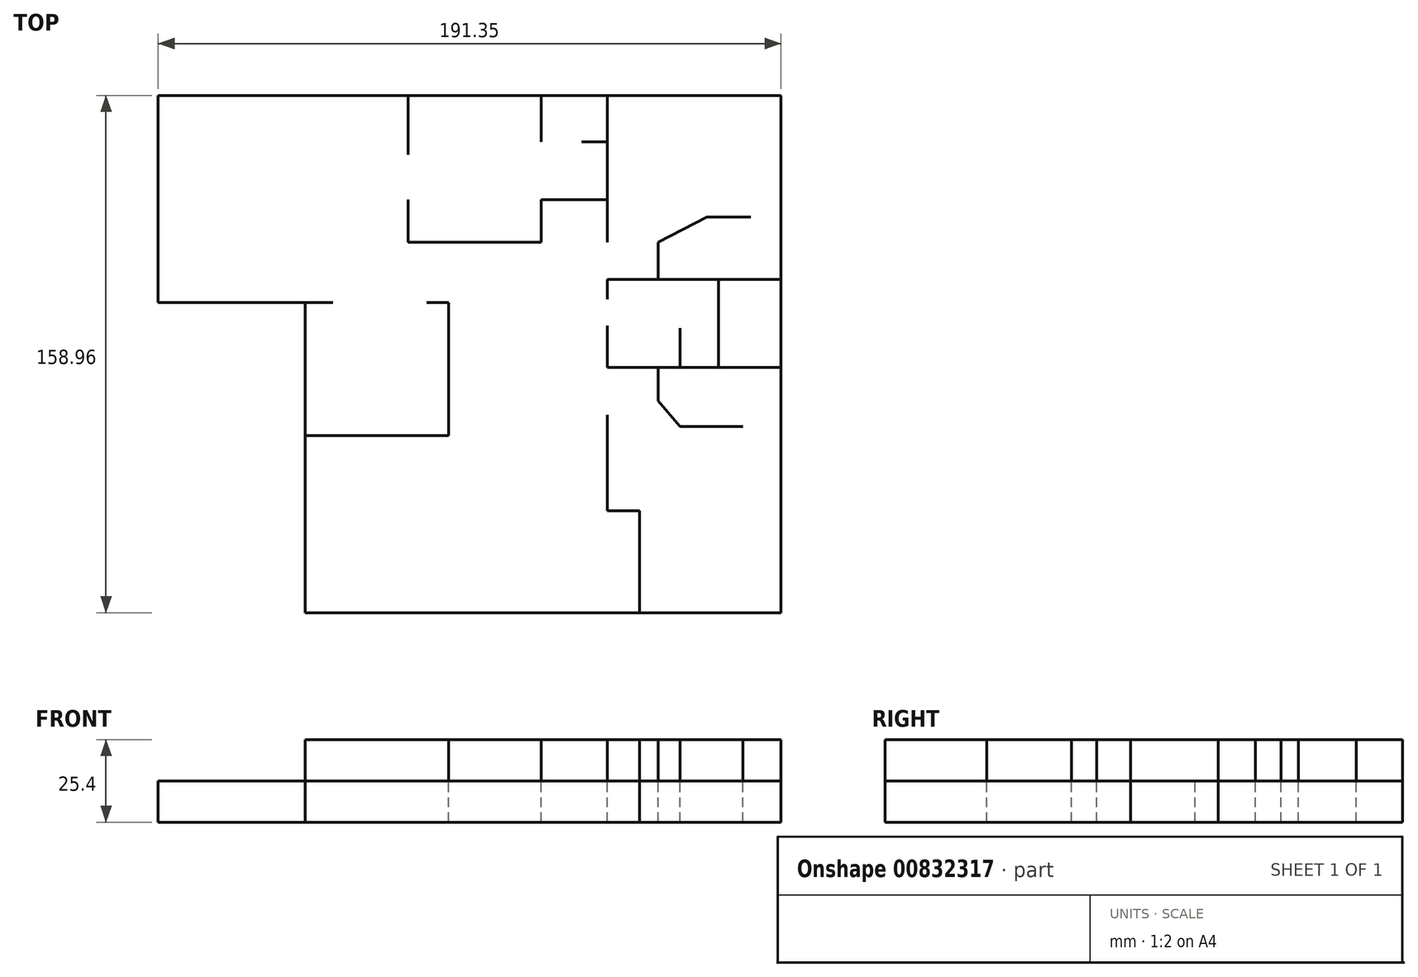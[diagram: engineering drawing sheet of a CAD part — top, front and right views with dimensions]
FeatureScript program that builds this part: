
annotation { "Feature Type Name" : "Feature", "Feature Type Description" : "" }
export const myFeature = defineFeature(function(context is Context, id is Id, definition is map)
    precondition{}
    {
        {
            var Q0;
            Q0=qCreatedBy(makeId("Top.planeOp"),FACE);
            var sketch = newSketch(context, id + "F0", { "sketchPlane" : qUnion([Q0])});
            skLineSegment(sketch, "E0", {"start": v(-96.38, 28.38) * mm, "end": v(94.97, 28.38) * mm});
            skLineSegment(sketch, "E1", {"start": v(94.97, 28.38) * mm, "end": v(94.97, -130.58) * mm});
            skLineSegment(sketch, "E2", {"start": v(94.97, -130.58) * mm, "end": v(-51.2, -130.58) * mm});
            skLineSegment(sketch, "E3", {"start": v(-51.2, -130.58) * mm, "end": v(-51.2, -35.27) * mm});
            skLineSegment(sketch, "E4", {"start": v(-51.2, -35.27) * mm, "end": v(-96.38, -35.27) * mm});
            skLineSegment(sketch, "E5", {"start": v(-96.38, -35.27) * mm, "end": v(-96.38, 28.38) * mm});
            skLineSegment(sketch, "E6", {"start": v(-51.2, -35.27) * mm, "end": v(-42.67, -35.27) * mm});
            skLineSegment(sketch, "E7", {"start": v(-51.2, -76.17) * mm, "end": v(-7.1, -76.17) * mm});
            skLineSegment(sketch, "E8", {"start": v(-7.1, -76.17) * mm, "end": v(-7.1, -35.27) * mm});
            skLineSegment(sketch, "E9", {"start": v(-7.1, -35.27) * mm, "end": v(-13.86, -35.27) * mm});
            skLineSegment(sketch, "E10", {"start": v(51.58, -99.29) * mm, "end": v(51.58, -130.58) * mm});
            skLineSegment(sketch, "E11", {"start": v(41.62, -99.29) * mm, "end": v(51.58, -99.29) * mm});
            skLineSegment(sketch, "E12", {"start": v(41.62, -69.77) * mm, "end": v(41.62, -99.29) * mm});
            skLineSegment(sketch, "E13", {"start": v(41.62, -99.29) * mm, "end": v(41.62, -69.77) * mm});
            skLineSegment(sketch, "E14", {"start": v(41.62, -42.39) * mm, "end": v(41.62, -55.19) * mm});
            skLineSegment(sketch, "E15", {"start": v(94.97, -55.19) * mm, "end": v(41.62, -55.19) * mm});
            skLineSegment(sketch, "E16", {"start": v(57.27, -55.19) * mm, "end": v(57.27, -65.5) * mm});
            skLineSegment(sketch, "E17", {"start": v(57.27, -65.5) * mm, "end": v(64.03, -73.33) * mm});
            skLineSegment(sketch, "E18", {"start": v(64.03, -73.33) * mm, "end": v(83.24, -73.33) * mm});
            skLineSegment(sketch, "E19", {"start": v(94.97, -28.16) * mm, "end": v(41.62, -28.16) * mm});
            skLineSegment(sketch, "E20", {"start": v(41.62, -28.16) * mm, "end": v(41.62, -34.2) * mm});
            skLineSegment(sketch, "E21", {"start": v(75.77, -28.16) * mm, "end": v(75.77, -55.19) * mm});
            skLineSegment(sketch, "E22", {"start": v(64.03, -43.1) * mm, "end": v(64.03, -55.19) * mm});
            skLineSegment(sketch, "E23", {"start": v(64.03, -55.19) * mm, "end": v(94.97, -55.19) * mm});
            skLineSegment(sketch, "E24", {"start": v(57.27, -28.16) * mm, "end": v(57.27, -16.78) * mm});
            skLineSegment(sketch, "E25", {"start": v(57.27, -16.78) * mm, "end": v(72.21, -8.96) * mm});
            skLineSegment(sketch, "E26", {"start": v(72.21, -8.96) * mm, "end": v(85.73, -8.96) * mm});
            skLineSegment(sketch, "E27", {"start": v(85.73, -8.96) * mm, "end": v(72.21, -8.96) * mm});
            skLineSegment(sketch, "E28", {"start": v(41.62, 28.38) * mm, "end": v(41.62, -16.78) * mm});
            skLineSegment(sketch, "E29", {"start": v(41.62, -3.62) * mm, "end": v(21.35, -3.62) * mm});
            skLineSegment(sketch, "E30", {"start": v(21.35, -3.62) * mm, "end": v(21.35, -16.78) * mm});
            skLineSegment(sketch, "E31", {"start": v(21.35, -16.78) * mm, "end": v(-19.55, -16.78) * mm});
            skLineSegment(sketch, "E32", {"start": v(-19.55, -16.78) * mm, "end": v(-19.55, -3.62) * mm});
            skLineSegment(sketch, "E33", {"start": v(-19.55, 10.25) * mm, "end": v(-19.55, 28.38) * mm});
            skLineSegment(sketch, "E34", {"start": v(21.35, 14.16) * mm, "end": v(21.35, 28.38) * mm});
            skLineSegment(sketch, "E35", {"start": v(33.8, 14.16) * mm, "end": v(41.62, 14.16) * mm});
            skPoint(sketch, "E35.endSnap0", {"position": v(41.62, 5.8) * mm});
            skSolve(sketch);
        }
        {
            var Q0;
            Q0=sQuery(id+"F0.wireOp",EDGE,"E0");
            var Q1;
            Q1=sQuery(id+"F0.wireOp",EDGE,"E5");
            var Q2;
            Q2=sQuery(id+"F0.wireOp",EDGE,"E4");
            var Q3;
            Q3=sQuery(id+"F0.wireOp",EDGE,"E3");
            var Q4;
            Q4=sQuery(id+"F0.wireOp",EDGE,"E2");
            var Q5;
            Q5=sQuery(id+"F0.wireOp",EDGE,"E1");
            extrude(context, id + "F1", {"bodyType" : ToolBodyType.SURFACE, "surfaceEntities" : qUnion([Q0, Q1, Q2, Q3, Q4, Q5]), "depth" : 12.7 * mm, "offsetDistance" : 25.4 * mm});
        }
        {
            var Q0;
            Q0=sQuery(id+"F0.wireOp",EDGE,"E6");
            var Q1;
            Q1=sQuery(id+"F0.wireOp",EDGE,"E7");
            var Q2;
            Q2=sQuery(id+"F0.wireOp",EDGE,"E8");
            var Q3;
            Q3=sQuery(id+"F0.wireOp",EDGE,"E9");
            extrude(context, id + "F2", {"bodyType" : ToolBodyType.SURFACE, "surfaceEntities" : qUnion([Q0, Q1, Q2, Q3]), "depth" : 25.4 * mm, "offsetDistance" : 25.4 * mm});
        }
        {
            var Q0;
            Q0=sQuery(id+"F0.wireOp",EDGE,"E32");
            var Q1;
            Q1=sQuery(id+"F0.wireOp",EDGE,"E31");
            var Q2;
            Q2=sQuery(id+"F0.wireOp",EDGE,"E30");
            var Q3;
            Q3=sQuery(id+"F0.wireOp",EDGE,"E29");
            extrude(context, id + "F3", {"bodyType" : ToolBodyType.SURFACE, "surfaceEntities" : qUnion([Q0, Q1, Q2, Q3]), "depth" : 25.4 * mm, "offsetDistance" : 25.4 * mm});
        }
        {
            var Q0;
            Q0=sQuery(id+"F0.wireOp",EDGE,"E34");
            var Q1;
            Q1=sQuery(id+"F0.wireOp",EDGE,"E35");
            extrude(context, id + "F4", {"bodyType" : ToolBodyType.SURFACE, "surfaceEntities" : qUnion([Q0, Q1]), "depth" : 25.4 * mm, "offsetDistance" : 25.4 * mm});
        }
        {
            var Q0;
            Q0=sQuery(id+"F0.wireOp",EDGE,"E33");
            var Q1;
            Q1=sQuery(id+"F0.wireOp",EDGE,"E28");
            extrude(context, id + "F5", {"bodyType" : ToolBodyType.SURFACE, "surfaceEntities" : qUnion([Q0, Q1]), "depth" : 25.4 * mm, "offsetDistance" : 25.4 * mm});
        }
        {
            var Q0;
            Q0=sQuery(id+"F0.wireOp",EDGE,"E25");
            var Q1;
            Q1=sQuery(id+"F0.wireOp",EDGE,"E26");
            var Q2;
            Q2=sQuery(id+"F0.wireOp",EDGE,"E24");
            extrude(context, id + "F6", {"bodyType" : ToolBodyType.SURFACE, "surfaceEntities" : qUnion([Q0, Q1, Q2]), "depth" : 25.4 * mm, "offsetDistance" : 25.4 * mm});
        }
        {
            var Q0;
            Q0=sQuery(id+"F0.wireOp",EDGE,"E19");
            extrude(context, id + "F7", {"bodyType" : ToolBodyType.SURFACE, "surfaceEntities" : qUnion([Q0]), "depth" : 25.4 * mm, "offsetDistance" : 25.4 * mm});
        }
        {
            var Q0;
            {var subQ5=sQuery(id+"F0.wireOp",EDGE,"E21");Q0=makeQuery(id+"F0.imprint","IMPRINT",FACE,{"disambiguationData":[TD([[makeQuery(id+"F0.imprint","IMPRINT",EDGE,{"derivedFrom":subQ5}),1.0]])]});}
            var Q1;
            Q1=sQuery(id+"F0.wireOp",EDGE,"E21");
            var Q2;
            Q2=sQuery(id+"F0.wireOp",EDGE,"E22");
            extrude(context, id + "F8", {"entities" : qUnion([Q0]), "bodyType" : ToolBodyType.SURFACE, "surfaceEntities" : qUnion([Q1, Q2]), "depth" : 25.4 * mm, "offsetDistance" : 25.4 * mm});
        }
        {
            var Q0;
            Q0=sQuery(id+"F0.wireOp",EDGE,"E20");
            var Q1;
            Q1=sQuery(id+"F0.wireOp",EDGE,"E14");
            var Q2;
            Q2=sQuery(id+"F0.wireOp",EDGE,"E16");
            var Q3;
            Q3=sQuery(id+"F0.wireOp",EDGE,"E17");
            var Q4;
            Q4=sQuery(id+"F0.wireOp",EDGE,"E18");
            var Q5;
            Q5=sQuery(id+"F0.wireOp",EDGE,"E12");
            var Q6;
            Q6=sQuery(id+"F0.wireOp",EDGE,"E11");
            var Q7;
            Q7=sQuery(id+"F0.wireOp",EDGE,"E10");
            extrude(context, id + "F9", {"bodyType" : ToolBodyType.SURFACE, "surfaceEntities" : qUnion([Q0, Q1, Q2, Q3, Q4, Q5, Q6, Q7]), "depth" : 25.4 * mm, "offsetDistance" : 25.4 * mm});
        }
        {
            var Q0;
            Q0=sQuery(id+"F0.wireOp",EDGE,"E15");
            extrude(context, id + "F10", {"bodyType" : ToolBodyType.SURFACE, "surfaceEntities" : qUnion([Q0]), "depth" : 25.4 * mm, "offsetDistance" : 25.4 * mm});
        }
    });
